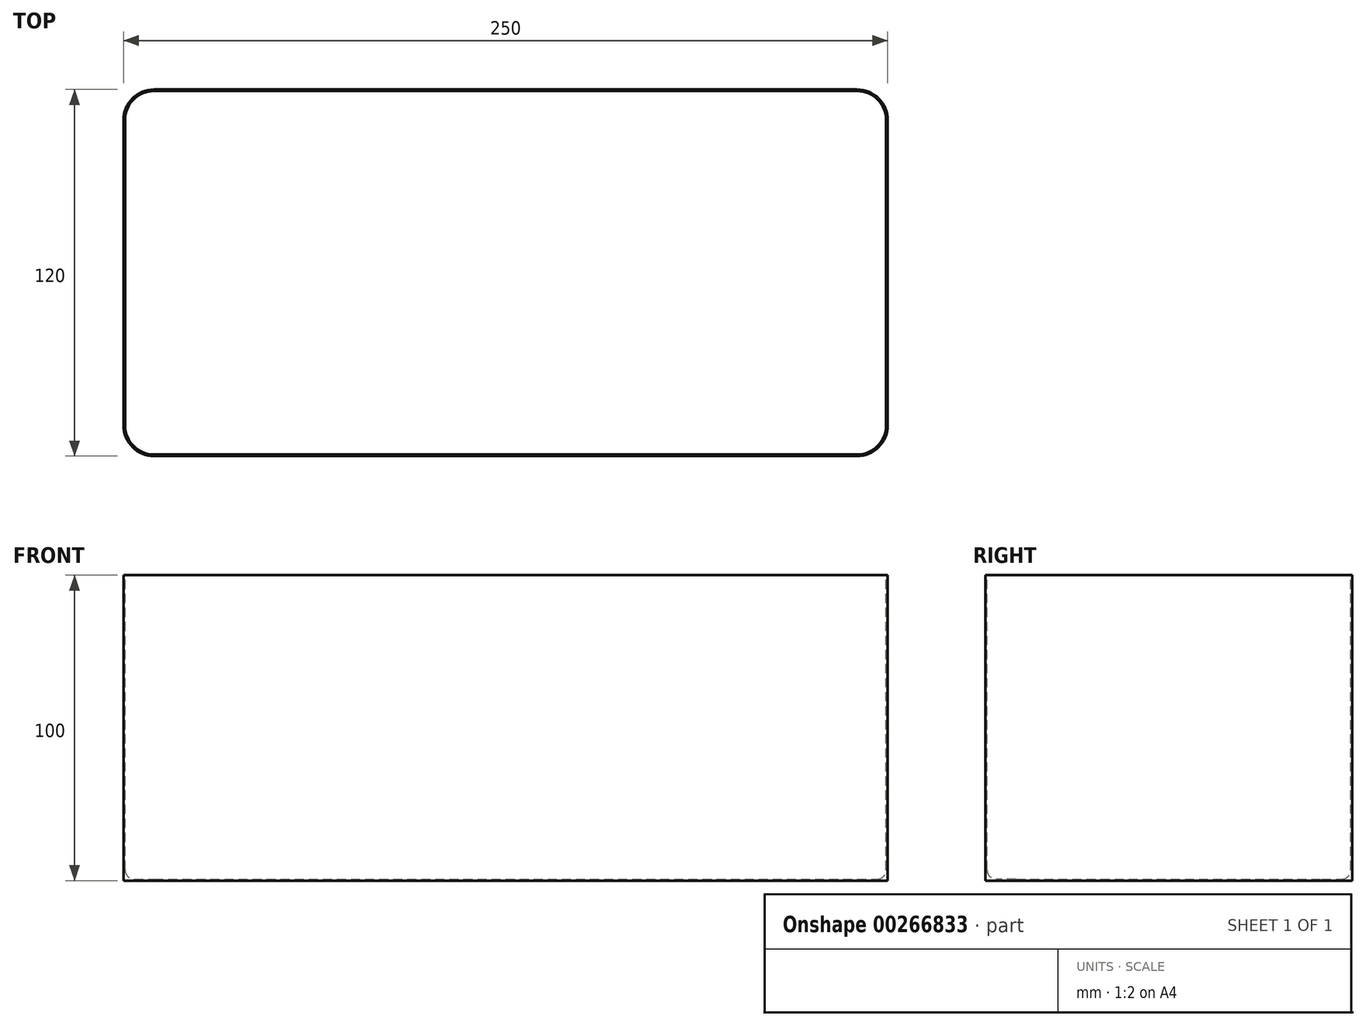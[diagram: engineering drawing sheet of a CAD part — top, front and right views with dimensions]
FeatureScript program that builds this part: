
annotation { "Feature Type Name" : "Feature", "Feature Type Description" : "" }
export const myFeature = defineFeature(function(context is Context, id is Id, definition is map)
    precondition{}
    {
        {
            var Q0;
            Q0=qCreatedBy(makeId("Top.planeOp"),FACE);
            var sketch = newSketch(context, id + "F0", { "sketchPlane" : qUnion([Q0])});
            skLineSegment(sketch, "E0.bottom", {"start": v(0, 0) * mm, "end": v(250, 0) * mm});
            skLineSegment(sketch, "E0.top", {"start": v(0, 120) * mm, "end": v(250, 120) * mm});
            skLineSegment(sketch, "E0.left", {"start": v(0, 0) * mm, "end": v(0, 120) * mm});
            skLineSegment(sketch, "E0.right", {"start": v(250, 0) * mm, "end": v(250, 120) * mm});
            skSolve(sketch);
        }
        {
            var Q0;
            Q0=makeQuery(id+"F0.imprint","IMPRINT",FACE,{"disambiguationData":[TD([[makeQuery(id+"F0.imprint","IMPRINT",EDGE,{"derivedFrom":sQuery(id+"F0.wireOp",EDGE,"E0.bottom")}),1.0]])]});
            extrude(context, id + "F1", {"entities" : qUnion([Q0]), "depth" : 100 * mm});
        }
        {
            var Q0;
            Q0=makeQuery(id+"F1.opExtrude","SWEPT_EDGE",EDGE,{"disambiguationData":[OSD([sQuery(id+"F0.wireOp",EDGE,"E0.bottom"),sQuery(id+"F0.wireOp",EDGE,"E0.left")])]});
            var Q1;
            Q1=makeQuery(id+"F1.opExtrude","SWEPT_EDGE",EDGE,{"disambiguationData":[OSD([sQuery(id+"F0.wireOp",EDGE,"E0.bottom"),sQuery(id+"F0.wireOp",EDGE,"E0.right")])]});
            var Q2;
            Q2=makeQuery(id+"F1.opExtrude","SWEPT_EDGE",EDGE,{"disambiguationData":[OSD([sQuery(id+"F0.wireOp",EDGE,"E0.top"),sQuery(id+"F0.wireOp",EDGE,"E0.right")])]});
            var Q3;
            Q3=makeQuery(id+"F1.opExtrude","SWEPT_EDGE",EDGE,{"disambiguationData":[OSD([sQuery(id+"F0.wireOp",EDGE,"E0.top"),sQuery(id+"F0.wireOp",EDGE,"E0.left")])]});
            fillet(context, id + "F2", {"entities" : qUnion([Q0, Q1, Q2, Q3]), "radius" : 10 * mm, "tangentPropagation" : true, "allowEdgeOverflow" : false});
        }
        {
            var Q0;
            Q0=makeQuery(id+"F1.opExtrude","CAP_FACE",FACE,{"disambiguationData":[OSD([sQuery(id+"F0.wireOp",EDGE,"E0.bottom"),sQuery(id+"F0.wireOp",EDGE,"E0.top"),sQuery(id+"F0.wireOp",EDGE,"E0.left"),sQuery(id+"F0.wireOp",EDGE,"E0.right")])],"isStart":false});
            shell(context, id + "F3", {"entities" : qUnion([Q0]), "thickness" : .5 * mm});
        }
        {
            var Q0;
            Q0=makeQuery(id+"F3.opShell","OFFSET_FACE",FACE,{"disambiguationData":[OSD([sQuery(id+"F0.wireOp",EDGE,"E0.bottom"),sQuery(id+"F0.wireOp",EDGE,"E0.top"),sQuery(id+"F0.wireOp",EDGE,"E0.left"),sQuery(id+"F0.wireOp",EDGE,"E0.right")])]});
            fillet(context, id + "F4", {"entities" : qUnion([Q0]), "radius" : 3 * mm, "tangentPropagation" : true, "allowEdgeOverflow" : false});
        }
    });
